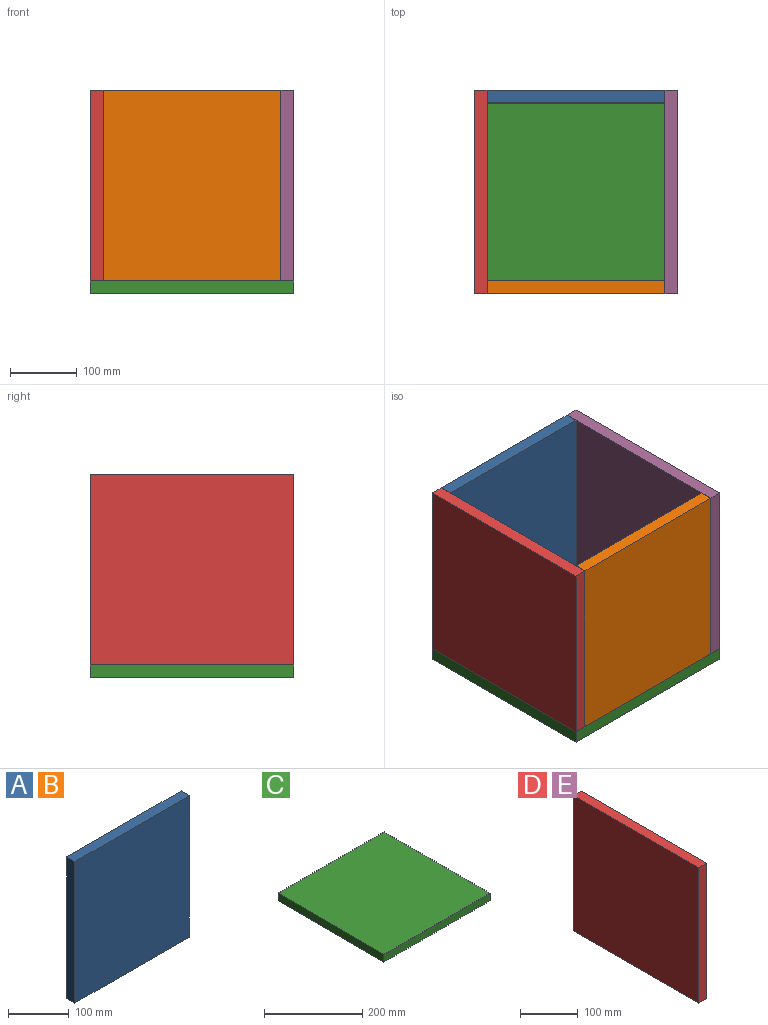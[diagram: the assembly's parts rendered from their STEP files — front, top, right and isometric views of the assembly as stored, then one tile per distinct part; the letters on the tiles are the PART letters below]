
ASSEMBLY  parts=5 mates=4
PART A: 6 faces, bbox 266.7x19.1x285.8 mm
  f0: plane 266.7x19.05mm, normal (0,0,-1), area 5080.6mm2, adj f1,f3,f4,f5
  f1: plane 285.75x19.05mm, normal (1,0,0), area 5443.5mm2, adj f0,f2,f4,f5
  f2: plane 266.7x19.05mm, normal (0,0,1), area 5080.6mm2, adj f1,f3,f4,f5
  f3: plane 285.75x19.05mm, normal (-1,0,0), area 5443.5mm2, adj f0,f2,f4,f5
  f4: plane 285.75x266.7mm, normal (0,-1,0), area 76209.5mm2, adj f0,f1,f2,f3
  f5: plane 285.75x266.7mm, normal (0,1,0), area 76209.5mm2, adj f0,f1,f2,f3
PART B: same geometry as A
PART C: 6 faces, bbox 304.8x304.8x19.1 mm
  f0: plane 304.8x19.05mm, normal (-1,0,0), area 5806.4mm2, adj f1,f3,f4,f5
  f1: plane 304.8x19.05mm, normal (0,-1,0), area 5806.4mm2, adj f0,f2,f4,f5
  f2: plane 304.8x19.05mm, normal (1,0,0), area 5806.4mm2, adj f1,f3,f4,f5
  f3: plane 304.8x19.05mm, normal (0,1,0), area 5806.4mm2, adj f0,f2,f4,f5
  f4: plane 304.8x304.8mm, normal (0,0,1), area 92903mm2, adj f0,f1,f2,f3
  f5: plane 304.8x304.8mm, normal (0,0,-1), area 92903mm2, adj f0,f1,f2,f3
PART D: 6 faces, bbox 19.1x304.8x285.8 mm
  f0: plane 304.8x19.05mm, normal (0,0,-1), area 5806.4mm2, adj f1,f3,f4,f5
  f1: plane 285.75x19.05mm, normal (0,1,0), area 5443.5mm2, adj f0,f2,f4,f5
  f2: plane 304.8x19.05mm, normal (0,0,1), area 5806.4mm2, adj f1,f3,f4,f5
  f3: plane 285.75x19.05mm, normal (0,-1,0), area 5443.5mm2, adj f0,f2,f4,f5
  f4: plane 304.8x285.75mm, normal (1,0,0), area 87096.6mm2, adj f0,f1,f2,f3
  f5: plane 304.8x285.75mm, normal (-1,0,0), area 87096.6mm2, adj f0,f1,f2,f3
PART E: same geometry as D
PLACE A t=(423.35,265.52,85.12)mm
PLACE B t=(423.35,-20.23,85.12)mm
PLACE C t=(423.35,113.12,-76.81)mm
PLACE D rot(axis=(0,0,-1),180deg) t=(290,113.12,85.12)mm
PLACE E t=(556.7,113.12,85.12)mm
MATE fastened E.f0 <-> C.f4  axis (0,0,-1) through (575.75,113.12,-57.76)mm
MATE fastened B.f0 <-> C.f4  axis (0,0,-1) through (423.35,-39.28,-57.76)mm
MATE fastened A.f0 <-> C.f4  axis (0,0,-1) through (423.35,265.52,-57.76)mm
MATE fastened D.f0 <-> C.f4  axis (0,0,-1) through (270.95,113.12,-57.76)mm
